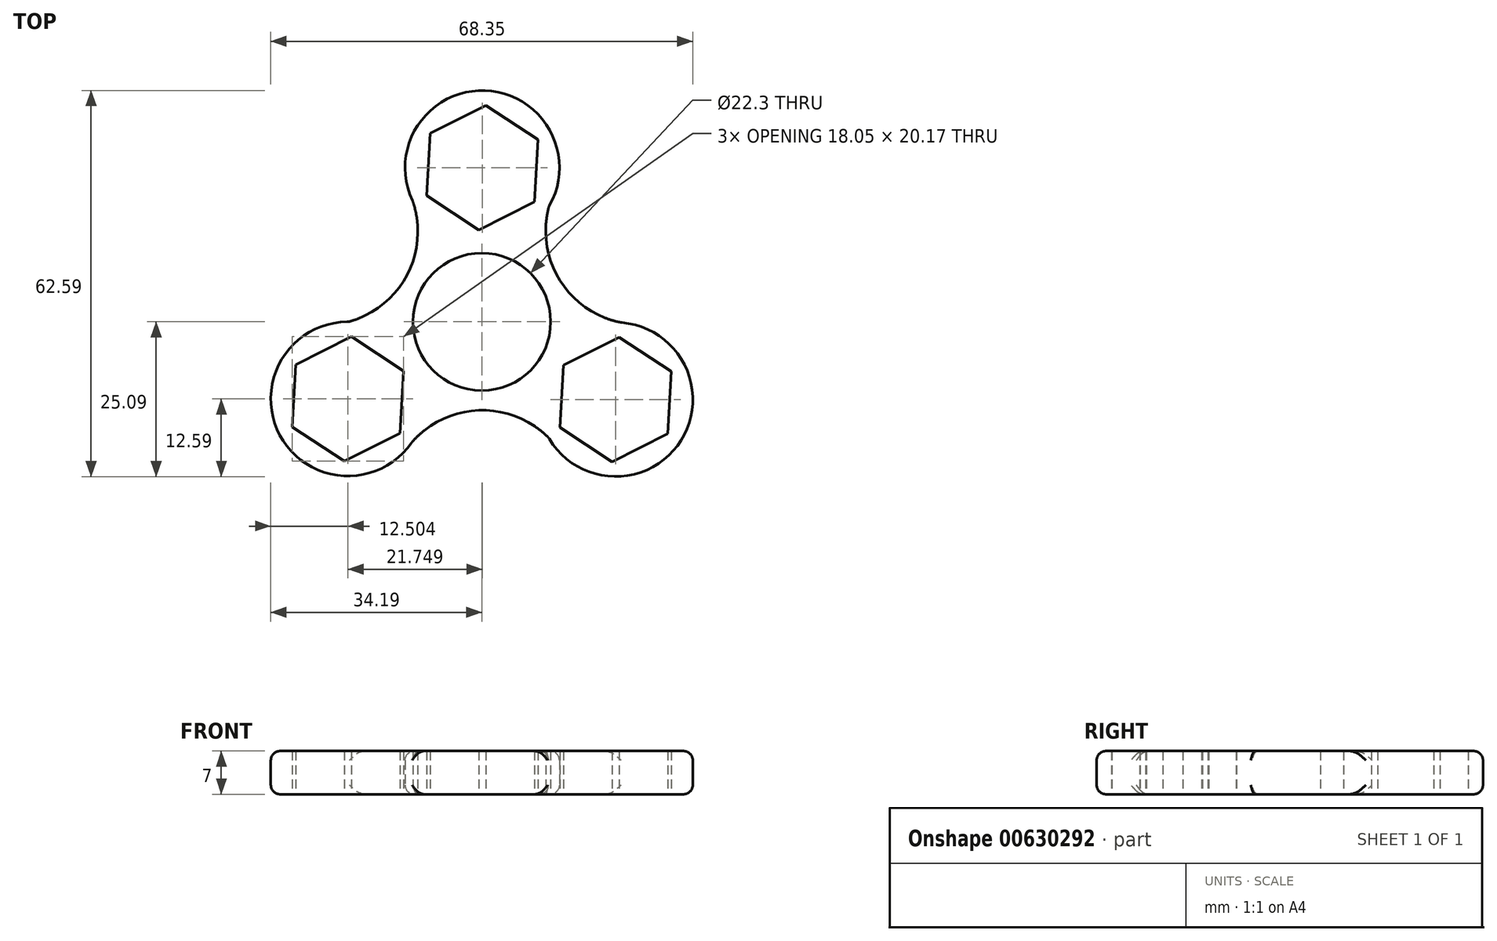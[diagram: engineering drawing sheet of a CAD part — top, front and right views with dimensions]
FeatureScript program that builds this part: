
annotation { "Feature Type Name" : "Feature", "Feature Type Description" : "" }
export const myFeature = defineFeature(function(context is Context, id is Id, definition is map)
    precondition{}
    {
        {
            var Q0;
            Q0=qCreatedBy(makeId("Top.planeOp"),FACE);
            var sketch = newSketch(context, id + "F0", { "sketchPlane" : qUnion([Q0])});
            skCircle(sketch, "E0", {"center": v(0, 0) * mm, "radius": 11.15 * mm});
            skCircle(sketch, "E1", {"center": v(0.06, 25) * mm, "radius": 12.5 * mm});
            skCircle(sketch, "E2.1.0", {"center": v(-21.69, -12.5) * mm, "radius": 12.5 * mm});
            skCircle(sketch, "E2.2.0", {"center": v(21.66, -12.59) * mm, "radius": 12.5 * mm});
            skArc(sketch, "E3", {"start": v(-21.65, 0) * mm, "mid": v(-11.8, 8.22) * mm, "end": v(-11.8, 21.04) * mm});
            skArc(sketch, "E4.1.0", {"start": v(10.82, -18.8) * mm, "mid": v(-1.22, -14.39) * mm, "end": v(-12.33, -20.8) * mm});
            skArc(sketch, "E4.2.0", {"start": v(10.87, 18.72) * mm, "mid": v(13.07, 6.08) * mm, "end": v(24.17, -0.34) * mm});
            skPoint(sketch, "E4.center", {"position": v(0.01, -0.03) * mm});
            skCircle(sketch, "E5.cCircle", {"center": v(0.06, 25) * mm, "radius": 8.75 * mm, "construction": true});
            skLineSegment(sketch, "E5.0", {"start": v(8.5, 19.45) * mm, "end": v(-0.52, 14.91) * mm});
            skLineSegment(sketch, "E5.1", {"start": v(-0.52, 14.91) * mm, "end": v(-8.96, 20.46) * mm});
            skLineSegment(sketch, "E5.2", {"start": v(-8.96, 20.46) * mm, "end": v(-8.38, 30.55) * mm});
            skLineSegment(sketch, "E5.3", {"start": v(-8.38, 30.55) * mm, "end": v(0.65, 35.09) * mm});
            skLineSegment(sketch, "E5.4", {"start": v(0.65, 35.09) * mm, "end": v(9.09, 29.54) * mm});
            skLineSegment(sketch, "E5.5", {"start": v(9.09, 29.54) * mm, "end": v(8.5, 19.45) * mm});
            skPoint(sketch, "E5.0.midPoint", {"position": v(4, 17.18) * mm});
            skCircle(sketch, "E6.1.0", {"center": v(-21.69, -12.5) * mm, "radius": 8.75 * mm, "construction": true});
            skLineSegment(sketch, "E6.1.1", {"start": v(-30.71, -17.04) * mm, "end": v(-30.13, -6.95) * mm});
            skLineSegment(sketch, "E6.1.2", {"start": v(-30.13, -6.95) * mm, "end": v(-21.1, -2.41) * mm});
            skLineSegment(sketch, "E6.1.3", {"start": v(-21.1, -2.41) * mm, "end": v(-12.66, -7.96) * mm});
            skLineSegment(sketch, "E6.1.4", {"start": v(-12.66, -7.96) * mm, "end": v(-13.24, -18.05) * mm});
            skLineSegment(sketch, "E6.1.5", {"start": v(-13.24, -18.05) * mm, "end": v(-22.27, -22.59) * mm});
            skLineSegment(sketch, "E6.1.6", {"start": v(-22.27, -22.59) * mm, "end": v(-30.71, -17.04) * mm});
            skCircle(sketch, "E6.2.0", {"center": v(21.66, -12.59) * mm, "radius": 8.75 * mm, "construction": true});
            skLineSegment(sketch, "E6.2.1", {"start": v(30.1, -18.13) * mm, "end": v(21.08, -22.67) * mm});
            skLineSegment(sketch, "E6.2.2", {"start": v(21.08, -22.67) * mm, "end": v(12.64, -17.12) * mm});
            skLineSegment(sketch, "E6.2.3", {"start": v(12.64, -17.12) * mm, "end": v(13.22, -7.04) * mm});
            skLineSegment(sketch, "E6.2.4", {"start": v(13.22, -7.04) * mm, "end": v(22.25, -2.5) * mm});
            skLineSegment(sketch, "E6.2.5", {"start": v(22.25, -2.5) * mm, "end": v(30.7, -8.05) * mm});
            skLineSegment(sketch, "E6.2.6", {"start": v(30.7, -8.05) * mm, "end": v(30.1, -18.13) * mm});
            skSolve(sketch);
        }
        {
            var Q0;
            Q0 = qSketchRegion(id + "F0", true);
            extrude(context, id + "F1", {"entities" : qUnion([Q0]), "depth" : 7 * mm, "offsetDistance" : 25 * mm});
        }
        {
            var Q0;
            Q0=makeQuery(id+"F1.opExtrude","SWEPT_FACE",FACE,{"disambiguationData":[OSD([sQuery(id+"F0.wireOp",EDGE,"E2.2.0")])]});
            var Q1;
            Q1=makeQuery(id+"F1.opExtrude","SWEPT_FACE",FACE,{"disambiguationData":[OSD([sQuery(id+"F0.wireOp",EDGE,"E1")])]});
            var Q2;
            Q2=makeQuery(id+"F1.opExtrude","SWEPT_FACE",FACE,{"disambiguationData":[OSD([sQuery(id+"F0.wireOp",EDGE,"E2.1.0")])]});
            fillet(context, id + "F2", {"entities" : qUnion([Q0, Q1, Q2]), "radius" : 1.5 * mm, "tangentPropagation" : true, "allowEdgeOverflow" : false});
        }
    });
